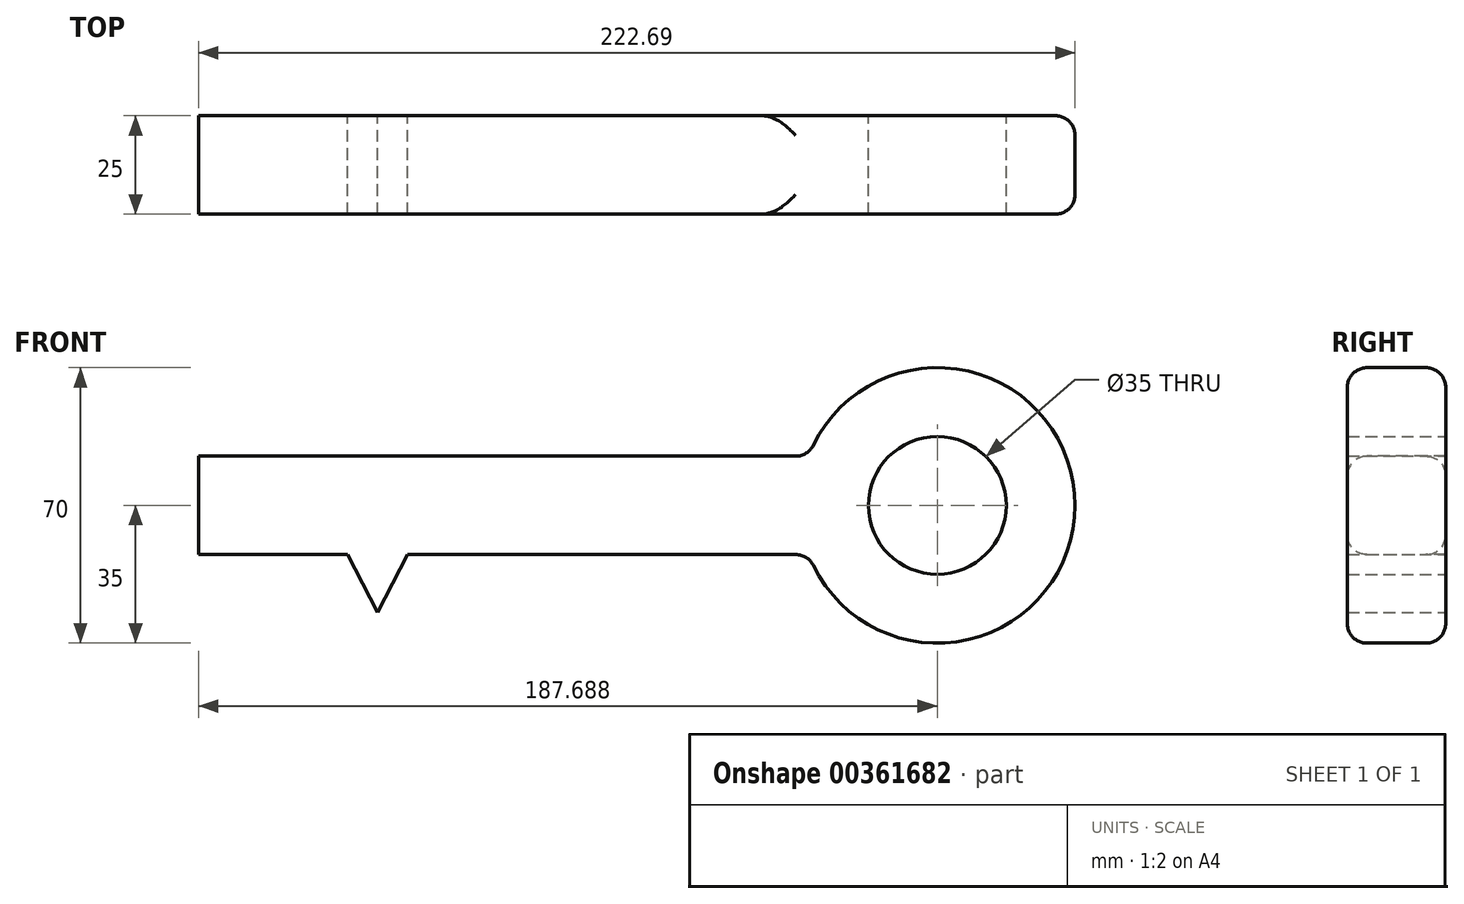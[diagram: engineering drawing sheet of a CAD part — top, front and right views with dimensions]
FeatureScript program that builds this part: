
annotation { "Feature Type Name" : "Feature", "Feature Type Description" : "" }
export const myFeature = defineFeature(function(context is Context, id is Id, definition is map)
    precondition{}
    {
        {
            var Q0;
            Q0=qCreatedBy(makeId("Front.planeOp"),FACE);
            var sketch = newSketch(context, id + "F0", { "sketchPlane" : qUnion([Q0])});
            skArc(sketch, "E0", {"start": v(25.04, -12.5) * mm, "mid": v(92.73, 0) * mm, "end": v(25.04, 12.5) * mm});
            skCircle(sketch, "E1", {"center": v(57.73, 0) * mm, "radius": 17.5 * mm});
            skLineSegment(sketch, "E2.bottom", {"start": v(25.04, 12.5) * mm, "end": v(-129.96, 12.5) * mm});
            skLineSegment(sketch, "E2.top", {"start": v(25.04, -12.5) * mm, "end": v(-129.96, -12.5) * mm});
            skLineSegment(sketch, "E2.right", {"start": v(-129.96, 12.5) * mm, "end": v(-129.96, -12.5) * mm});
            skPoint(sketch, "E2.middle", {"position": v(-52.46, 0) * mm});
            skLineSegment(sketch, "E3.bottom", {"start": v(-129.96, -12.5) * mm, "end": v(-119.96, -12.5) * mm});
            skLineSegment(sketch, "E3.top", {"start": v(-129.96, -42.5) * mm, "end": v(-119.96, -42.5) * mm});
            skLineSegment(sketch, "E3.left", {"start": v(-129.96, -12.5) * mm, "end": v(-129.96, -42.5) * mm});
            skLineSegment(sketch, "E3.right", {"start": v(-119.96, -12.5) * mm, "end": v(-119.96, -42.5) * mm});
            skLineSegment(sketch, "E4.bottom", {"start": v(-109.96, -12.5) * mm, "end": v(-101.96, -12.5) * mm});
            skLineSegment(sketch, "E4.top", {"start": v(-109.96, -27.5) * mm, "end": v(-101.96, -27.5) * mm});
            skLineSegment(sketch, "E4.left", {"start": v(-109.96, -12.5) * mm, "end": v(-109.96, -27.5) * mm});
            skLineSegment(sketch, "E4.right", {"start": v(-101.96, -12.5) * mm, "end": v(-101.96, -27.5) * mm});
            skPoint(sketch, "E5.startSnap0", {"position": v(-109.96, -20) * mm});
            skPoint(sketch, "E6.endSnap0", {"position": v(-101.96, -20) * mm});
            skLineSegment(sketch, "E7", {"start": v(-92.13, -12.5) * mm, "end": v(-84.52, -27.2) * mm});
            skLineSegment(sketch, "E8", {"start": v(-84.52, -27.2) * mm, "end": v(-76.9, -12.5) * mm});
            skSolve(sketch);
        }
        {
            var Q0;
            {var subQ1=sQuery(id+"F0.wireOp",EDGE,"E0");Q0=makeQuery(id+"F0.imprint","IMPRINT",FACE,{"disambiguationData":[TD([[makeQuery(id+"F0.imprint","IMPRINT",EDGE,{"derivedFrom":subQ1}),1.0]])]});}
            var Q1;
            Q1=makeQuery(id+"F0.imprint","IMPRINT",FACE,{"disambiguationData":[TD([[makeQuery(id+"F0.imprint","IMPRINT",EDGE,{"derivedFrom":sQuery(id+"F0.wireOp",EDGE,"E3.bottom")}),-1.0]])]});
            var Q2;
            Q2=makeQuery(id+"F0.imprint","IMPRINT",FACE,{"disambiguationData":[TD([[makeQuery(id+"F0.imprint","IMPRINT",EDGE,{"derivedFrom":sQuery(id+"F0.wireOp",EDGE,"E4.bottom")}),-1.0]])]});
            var Q3;
            {var subQ0=sQuery(id+"F0.wireOp",EDGE,"E7");Q3=makeQuery(id+"F0.imprint","IMPRINT",FACE,{"disambiguationData":[TD([[makeQuery(id+"F0.imprint","IMPRINT",EDGE,{"derivedFrom":subQ0}),1.0]])]});}
            extrude(context, id + "F1", {"entities" : qUnion([Q0, Q1, Q2, Q3]), "depth" : 25 * mm});
        }
        {
            var Q0;
            Q0=makeQuery(id+"F1.opExtrude","SWEPT_FACE",FACE,{"disambiguationData":[OSD([sQuery(id+"F0.wireOp",EDGE,"E0")])]});
            fillet(context, id + "F2", {"entities" : qUnion([Q0]), "radius" : 5 * mm, "tangentPropagation" : true, "allowEdgeOverflow" : false});
        }
    });
